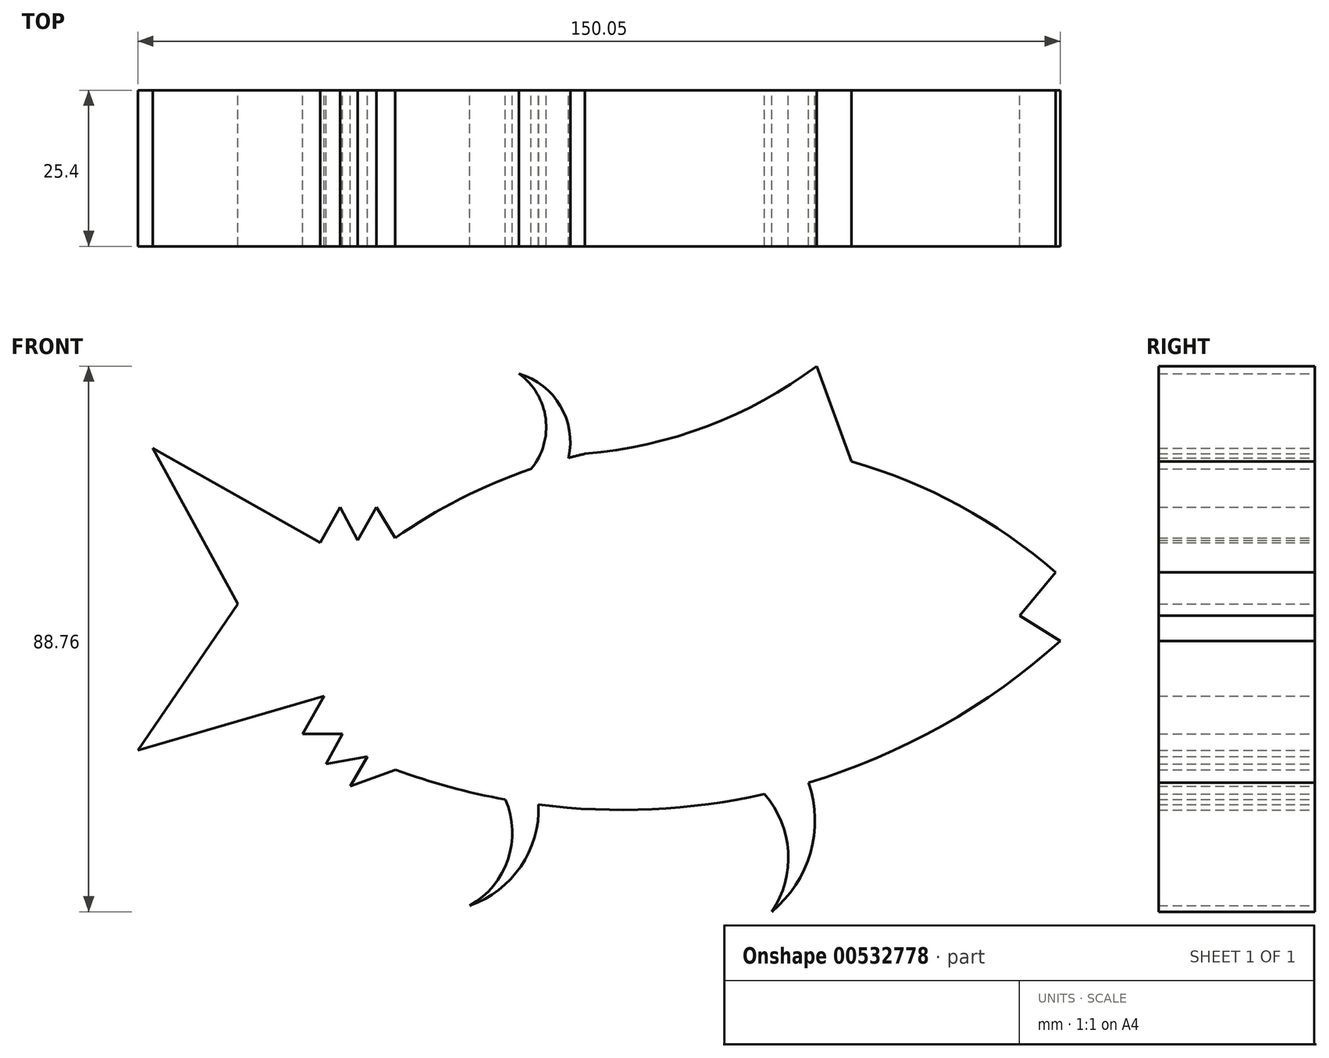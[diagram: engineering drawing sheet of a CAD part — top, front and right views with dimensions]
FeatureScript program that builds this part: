
annotation { "Feature Type Name" : "Feature", "Feature Type Description" : "" }
export const myFeature = defineFeature(function(context is Context, id is Id, definition is map)
    precondition{}
    {
        {
            var Q0;
            Q0=qCreatedBy(makeId("Front.planeOp"),FACE);
            var sketch = newSketch(context, id + "F0", { "sketchPlane" : qUnion([Q0])});
            skLineSegment(sketch, "E0", {"start": v(-73.44, 37.7) * mm, "end": v(-59.58, 12.4) * mm});
            skLineSegment(sketch, "E1", {"start": v(-59.58, 12.4) * mm, "end": v(-75.88, -11.43) * mm});
            skLineSegment(sketch, "E2", {"start": v(-73.44, 37.7) * mm, "end": v(-46.2, 22.37) * mm});
            skArc(sketch, "E3", {"start": v(73.44, 17.5) * mm, "mid": v(20.68, 38.85) * mm, "end": v(-34.02, 23.1) * mm});
            skArc(sketch, "E4", {"start": v(-36.48, -13.62) * mm, "mid": v(21.7, -19.43) * mm, "end": v(74.17, 6.38) * mm});
            skLineSegment(sketch, "E5", {"start": v(-45.6, -2.6) * mm, "end": v(-75.88, -11.43) * mm});
            skLineSegment(sketch, "E6", {"start": v(40.23, 35.57) * mm, "end": v(34.53, 51.07) * mm});
            skArc(sketch, "E7", {"start": v(-3.13, 36.8) * mm, "mid": v(16.7, 41.29) * mm, "end": v(34.53, 51.07) * mm});
            skLineSegment(sketch, "E8", {"start": v(74.17, 6.38) * mm, "end": v(67.6, 10.46) * mm});
            skLineSegment(sketch, "E9", {"start": v(67.6, 10.46) * mm, "end": v(73.44, 17.5) * mm});
            skCircle(sketch, "E10", {"center": v(53.99, 20.91) * mm, "radius": 2.77 * mm});
            skArc(sketch, "E11", {"start": v(27.24, -37.7) * mm, "mid": v(33.54, -28.12) * mm, "end": v(33.23, -16.67) * mm});
            skArc(sketch, "E12", {"start": v(27.24, -37.7) * mm, "mid": v(29.9, -27.92) * mm, "end": v(26.05, -18.55) * mm});
            skArc(sketch, "E13", {"start": v(-5.81, 36.16) * mm, "mid": v(-7.13, 44.6) * mm, "end": v(-13.86, 49.85) * mm});
            skArc(sketch, "E14", {"start": v(-11.9, 34.34) * mm, "mid": v(-9.53, 42.52) * mm, "end": v(-13.86, 49.85) * mm});
            skArc(sketch, "E15", {"start": v(-21.89, -36.72) * mm, "mid": v(-13.59, -30.33) * mm, "end": v(-10.68, -20.27) * mm});
            skArc(sketch, "E16", {"start": v(-21.89, -36.72) * mm, "mid": v(-15.68, -29.2) * mm, "end": v(-16.08, -19.44) * mm});
            skArc(sketch, "E17", {"start": v(-45.6, -2.6) * mm, "mid": v(-42.27, -9.12) * mm, "end": v(-36.48, -13.62) * mm});
            skLineSegment(sketch, "E18", {"start": v(-46.2, 22.37) * mm, "end": v(-34.02, 23.1) * mm});
            skLineSegment(sketch, "E19", {"start": v(-46.2, 22.37) * mm, "end": v(-42.97, 28.14) * mm});
            skLineSegment(sketch, "E20", {"start": v(-42.97, 28.14) * mm, "end": v(-40.11, 22.74) * mm});
            skLineSegment(sketch, "E21", {"start": v(-40.11, 22.74) * mm, "end": v(-37.08, 28.14) * mm});
            skLineSegment(sketch, "E22", {"start": v(-37.08, 28.14) * mm, "end": v(-34.02, 23.1) * mm});
            skLineSegment(sketch, "E23", {"start": v(-45.6, -2.6) * mm, "end": v(-49.07, -8.76) * mm});
            skLineSegment(sketch, "E24", {"start": v(-42.57, -8.76) * mm, "end": v(-45.23, -13.62) * mm});
            skLineSegment(sketch, "E25", {"start": v(-45.23, -13.62) * mm, "end": v(-38.55, -12.46) * mm});
            skLineSegment(sketch, "E26", {"start": v(-38.55, -12.46) * mm, "end": v(-41.34, -17.27) * mm});
            skLineSegment(sketch, "E27", {"start": v(-41.34, -17.27) * mm, "end": v(-33.95, -14.58) * mm});
            skLineSegment(sketch, "E28", {"start": v(-49.07, -8.76) * mm, "end": v(-42.57, -8.76) * mm});
            skSolve(sketch);
        }
        {
            var Q0;
            {var subQ0=sQuery(id+"F0.wireOp",EDGE,"E6");Q0=makeQuery(id+"F0.imprint","IMPRINT",FACE,{"disambiguationData":[TD([[makeQuery(id+"F0.imprint","IMPRINT",EDGE,{"derivedFrom":subQ0}),1.0]])]});}
            var Q1;
            {var subQ0=sQuery(id+"F0.wireOp",EDGE,"E13");Q1=makeQuery(id+"F0.imprint","IMPRINT",FACE,{"disambiguationData":[TD([[makeQuery(id+"F0.imprint","IMPRINT",EDGE,{"derivedFrom":subQ0}),1.0]])]});}
            var Q2;
            {var subQ4=sQuery(id+"F0.wireOp",EDGE,"E26");Q2=makeQuery(id+"F0.imprint","IMPRINT",FACE,{"disambiguationData":[TD([[makeQuery(id+"F0.imprint","IMPRINT",EDGE,{"derivedFrom":subQ4}),1.0]])]});}
            var Q3;
            {var subQ0=sQuery(id+"F0.wireOp",EDGE,"E15");Q3=makeQuery(id+"F0.imprint","IMPRINT",FACE,{"disambiguationData":[TD([[makeQuery(id+"F0.imprint","IMPRINT",EDGE,{"derivedFrom":subQ0}),1.0]])]});}
            var Q4;
            {var subQ0=sQuery(id+"F0.wireOp",EDGE,"E11");Q4=makeQuery(id+"F0.imprint","IMPRINT",FACE,{"disambiguationData":[TD([[makeQuery(id+"F0.imprint","IMPRINT",EDGE,{"derivedFrom":subQ0}),1.0]])]});}
            var Q5;
            Q5=makeQuery(id+"F0.imprint","IMPRINT",FACE,{"disambiguationData":[TD([[makeQuery(id+"F0.imprint","IMPRINT",EDGE,{"derivedFrom":sQuery(id+"F0.wireOp",EDGE,"E10")}),1.0]])]});
            var Q6;
            {var subQ0=sQuery(id+"F0.wireOp",EDGE,"E23");Q6=makeQuery(id+"F0.imprint","IMPRINT",FACE,{"disambiguationData":[TD([[makeQuery(id+"F0.imprint","IMPRINT",EDGE,{"derivedFrom":subQ0}),1.0]])]});}
            var Q7;
            {var subQ0=sQuery(id+"F0.wireOp",EDGE,"E24");Q7=makeQuery(id+"F0.imprint","IMPRINT",FACE,{"disambiguationData":[TD([[makeQuery(id+"F0.imprint","IMPRINT",EDGE,{"derivedFrom":subQ0}),1.0]])]});}
            var Q8;
            {var subQ0=sQuery(id+"F0.wireOp",EDGE,"E19");Q8=makeQuery(id+"F0.imprint","IMPRINT",FACE,{"disambiguationData":[TD([[makeQuery(id+"F0.imprint","IMPRINT",EDGE,{"derivedFrom":subQ0}),-1.0]])]});}
            var Q9;
            {var subQ2=sQuery(id+"F0.wireOp",EDGE,"E21");Q9=makeQuery(id+"F0.imprint","IMPRINT",FACE,{"disambiguationData":[TD([[makeQuery(id+"F0.imprint","IMPRINT",EDGE,{"derivedFrom":subQ2}),-1.0]])]});}
            var Q10;
            Q10=makeQuery(id+"F0.imprint","IMPRINT",FACE,{"disambiguationData":[TD([[makeQuery(id+"F0.imprint","IMPRINT",EDGE,{"derivedFrom":sQuery(id+"F0.wireOp",EDGE,"E0")}),1.0]])]});
            var Q11;
            {var subQ0=sQuery(id+"F0.wireOp",EDGE,"E7");var subQ1=sQuery(id+"F0.wireOp",EDGE,"E3");var subQ2=makeQuery(id+"F0.imprint","INTERSECT",VERTEX,{"disambiguationData":[OD(0.0)],"derivedFrom":[subQ1,subQ0]});Q11=makeQuery(id+"F0.imprint","IMPRINT",FACE,{"disambiguationData":[TD([[makeQuery(id+"F0.imprint","IMPRINT",EDGE,{"disambiguationData":[TD([[subQ2,1.0]])],"derivedFrom":subQ1}),1.0]])]});}
            extrude(context, id + "F1", {"entities" : qUnion([Q0, Q1, Q2, Q3, Q4, Q5, Q6, Q7, Q8, Q9, Q10, Q11]), "depth" : 25.4 * mm, "offsetDistance" : 25.4 * mm});
        }
    });
